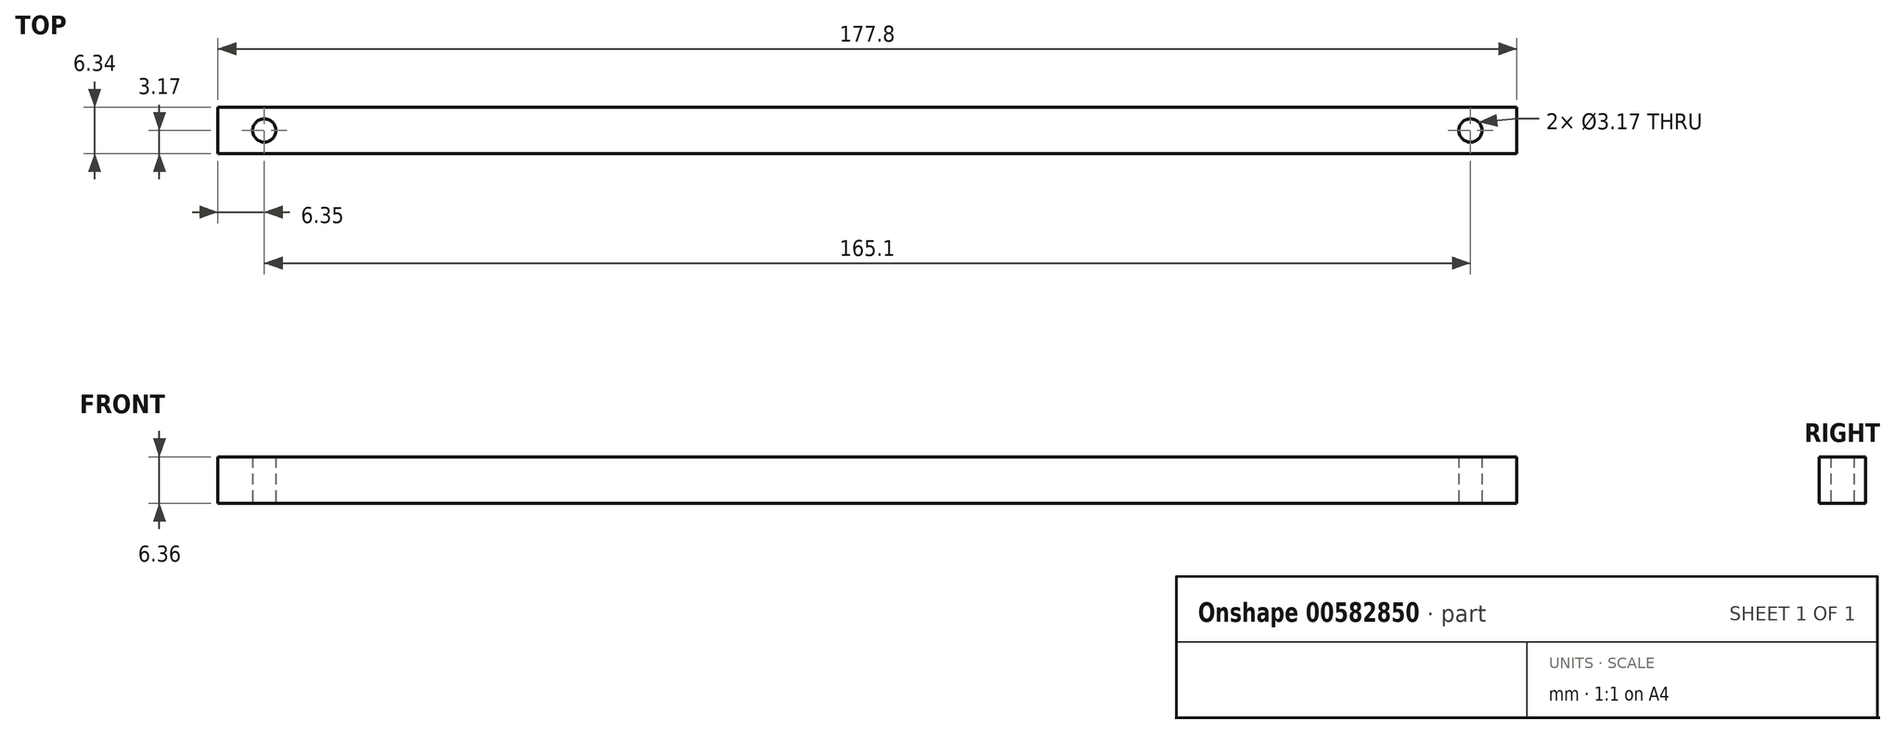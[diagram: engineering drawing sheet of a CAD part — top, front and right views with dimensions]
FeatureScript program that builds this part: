
annotation { "Feature Type Name" : "Feature", "Feature Type Description" : "" }
export const myFeature = defineFeature(function(context is Context, id is Id, definition is map)
    precondition{}
    {
        {
            var Q0;
            Q0=qCreatedBy(makeId("Top.planeOp"),FACE);
            var sketch = newSketch(context, id + "F0", { "sketchPlane" : qUnion([Q0])});
            skLineSegment(sketch, "E0.bottom", {"start": v(-88.9, -3.18) * mm, "end": v(88.9, -3.18) * mm});
            skLineSegment(sketch, "E0.top", {"start": v(-88.9, 3.18) * mm, "end": v(88.9, 3.18) * mm});
            skLineSegment(sketch, "E0.left", {"start": v(-88.9, -3.18) * mm, "end": v(-88.9, 3.18) * mm});
            skLineSegment(sketch, "E0.right", {"start": v(88.9, -3.18) * mm, "end": v(88.9, 3.18) * mm});
            skPoint(sketch, "E0.middle", {"position": v(0, 0) * mm});
            skCircle(sketch, "E1", {"center": v(82.55, 0) * mm, "radius": 1.59 * mm});
            skCircle(sketch, "E2", {"center": v(-82.55, 0) * mm, "radius": 1.59 * mm});
            skSolve(sketch);
        }
        {
            var Q0;
            Q0=makeQuery(id+"F0.imprint","IMPRINT",FACE,{"disambiguationData":[TD([[makeQuery(id+"F0.imprint","IMPRINT",EDGE,{"derivedFrom":sQuery(id+"F0.wireOp",EDGE,"E0.bottom")}),1.0]])]});
            extrude(context, id + "F1", {"entities" : qUnion([Q0]), "endBound" : BoundingType.SYMMETRIC, "depth" : 6.35 * mm, "offsetDistance" : 25.4 * mm});
        }
    });
